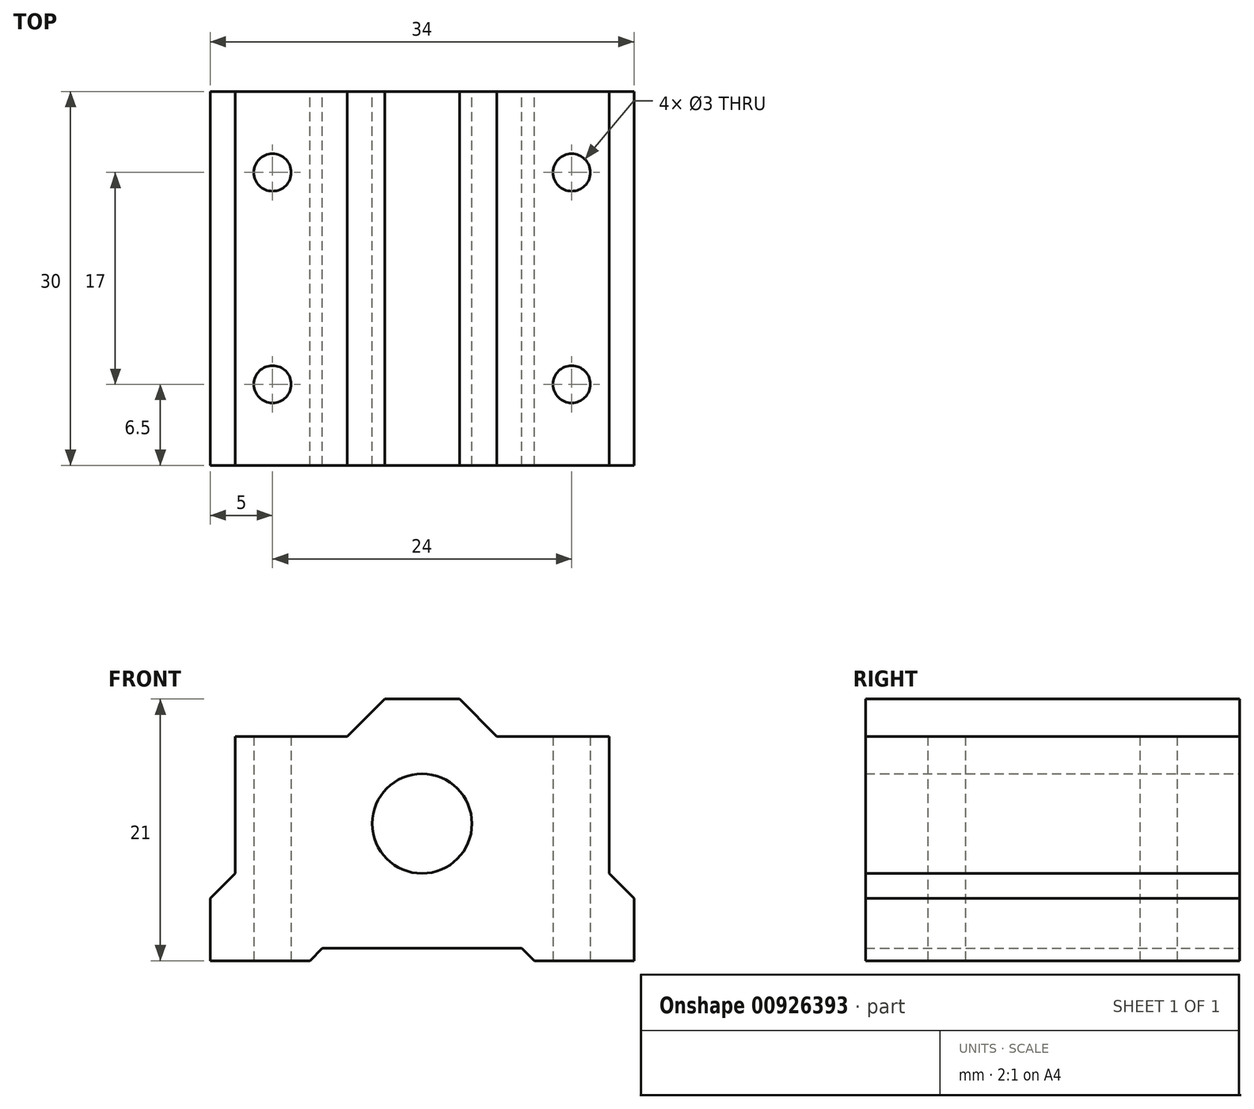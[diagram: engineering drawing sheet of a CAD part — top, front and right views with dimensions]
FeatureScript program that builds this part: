
annotation { "Feature Type Name" : "Feature", "Feature Type Description" : "" }
export const myFeature = defineFeature(function(context is Context, id is Id, definition is map)
    precondition{}
    {
        {
            var Q0;
            Q0=qCreatedBy(makeId("Front.planeOp"),FACE);
            var sketch = newSketch(context, id + "F0", { "sketchPlane" : qUnion([Q0])});
            skLineSegment(sketch, "E0", {"start": v(0, 21) * mm, "end": v(0, 0) * mm, "construction": true});
            skLineSegment(sketch, "E1", {"start": v(0, 1) * mm, "end": v(8, 1) * mm});
            skLineSegment(sketch, "E2", {"start": v(8, 1) * mm, "end": v(9, 0) * mm});
            skLineSegment(sketch, "E3", {"start": v(9, 0) * mm, "end": v(17, 0) * mm});
            skLineSegment(sketch, "E4", {"start": v(17, 0) * mm, "end": v(17, 5) * mm});
            skLineSegment(sketch, "E5", {"start": v(17, 5) * mm, "end": v(15, 7) * mm});
            skLineSegment(sketch, "E6", {"start": v(15, 7) * mm, "end": v(15, 18) * mm});
            skLineSegment(sketch, "E7", {"start": v(15, 18) * mm, "end": v(6, 18) * mm});
            skLineSegment(sketch, "E8", {"start": v(6, 18) * mm, "end": v(3, 21) * mm});
            skLineSegment(sketch, "E9", {"start": v(3, 21) * mm, "end": v(0, 21) * mm});
            skArc(sketch, "E10", {"start": v(0, 7) * mm, "mid": v(4, 11) * mm, "end": v(0, 15) * mm});
            skLineSegment(sketch, "E11.MirrorCS", {"start": v(-8, 1) * mm, "end": v(-9, 0) * mm});
            skLineSegment(sketch, "E12.MirrorCS", {"start": v(-17, 0) * mm, "end": v(-17, 5) * mm});
            skLineSegment(sketch, "E13.MirrorCS", {"start": v(0, 1) * mm, "end": v(-8, 1) * mm});
            skLineSegment(sketch, "E14.MirrorCS", {"start": v(-15, 18) * mm, "end": v(-6, 18) * mm});
            skLineSegment(sketch, "E15.MirrorCS", {"start": v(-3, 21) * mm, "end": v(0, 21) * mm});
            skLineSegment(sketch, "E16.MirrorCS", {"start": v(-15, 7) * mm, "end": v(-15, 18) * mm});
            skArc(sketch, "E17.MirrorCS", {"start": v(0, 7) * mm, "mid": v(-4, 11) * mm, "end": v(0, 15) * mm});
            skLineSegment(sketch, "E18.MirrorCS", {"start": v(-6, 18) * mm, "end": v(-3, 21) * mm});
            skLineSegment(sketch, "E19.MirrorCS", {"start": v(-9, 0) * mm, "end": v(-17, 0) * mm});
            skLineSegment(sketch, "E20.MirrorCS", {"start": v(-17, 5) * mm, "end": v(-15, 7) * mm});
            skSolve(sketch);
        }
        {
            var Q0;
            Q0 = qSketchRegion(id + "F0", true);
            extrude(context, id + "F1", {"entities" : qUnion([Q0]), "depth" : 30 * mm, "offsetDistance" : 25 * mm});
        }
        {
            var Q0;
            Q0=qCreatedBy(makeId("Top.planeOp"),FACE);
            var sketch = newSketch(context, id + "F2", { "sketchPlane" : qUnion([Q0])});
            skCircle(sketch, "E21", {"center": v(-12, -6.5) * mm, "radius": 1.5 * mm});
            skLineSegment(sketch, "E22", {"start": v(0, 0) * mm, "end": v(0, -30) * mm, "construction": true});
            skLineSegment(sketch, "E23", {"start": v(-17, -15) * mm, "end": v(17, -15) * mm, "construction": true});
            skCircle(sketch, "E24.MirrorC", {"center": v(-12, -23.5) * mm, "radius": 1.5 * mm});
            skCircle(sketch, "E25.MirrorC", {"center": v(12, -23.5) * mm, "radius": 1.5 * mm});
            skCircle(sketch, "E26.MirrorC", {"center": v(12, -6.5) * mm, "radius": 1.5 * mm});
            skSolve(sketch);
        }
        {
            var Q0;
            Q0 = qSketchRegion(id + "F2", true);
            extrude(context, id + "F3", {"entities" : qUnion([Q0]), "operationType" : NewBodyOperationType.REMOVE, "endBound" : BoundingType.THROUGH_ALL, "depth" : 25 * mm, "offsetDistance" : 25 * mm});
        }
    });
